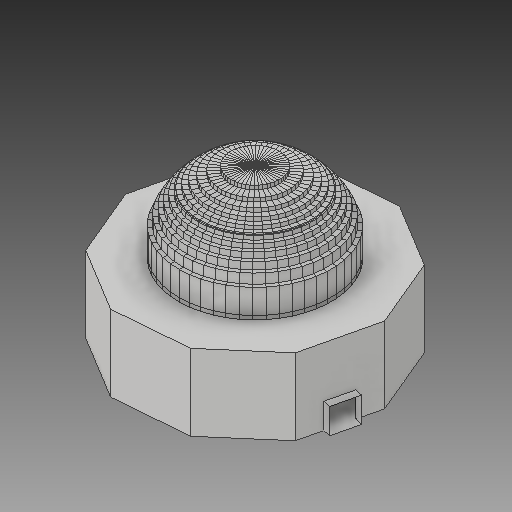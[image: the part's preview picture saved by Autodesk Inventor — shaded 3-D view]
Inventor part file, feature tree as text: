
AUTODESK INVENTOR PART (.ipt)
format: ipt  version: 2017 (Build 210142000, 142)  size: 2,418,176 bytes
history: native  units: in
note: dims shown in document units (in); Inventor stores cm internally (conversion verified against a paired STEP export)
features: extrude x8, sketch x7, other x3, plane x1, pattern_circular x1
ambient origin geometry x8: Origin, YZ Plane, XZ Plane, XY Plane, X Axis, Y Axis, Z Axis, Center Point
bodies: Solid1 (feature_tree)
feature tree (20):
  extrude  "bace"  Depth=1.0in TaperAngle=0.0deg
  extrude  "bace wall"  Depth=20.0in TaperAngle=0.0deg
  extrude  "bace ceiling"  Depth=1.0in
  other  "used to find the workplane for the dome"
  plane  "workplane for dome"
  extrude  "dome make"  Depth=1.0in TaperAngle=0.0deg
  sketch  "Sketch18"  dims[d190=45.0deg d192=1.0in d193=1.0in d194=1.0in d195=1.0in d196=1.0in d197=1.0in d198=1.0in d199=1.0in d200=0.0in d201=1.0in d202=0.0in d204=1.0in d205=19.685in d206=360.0deg d208=1.0in]
  extrude  "dome part cut 1"  Depth=2.5166in TaperAngle=90.0deg
  extrude  "dome part cut 2"  Depth=21.0in
  pattern_circular  "Circular Pattern6"  [2 undecoded]
  extrude  "door frame"  Depth=1.0in
  extrude  "corridor connection"  Depth=1.0in
  other  "Delete Faces of the room"
  other  "Delete Faces of dome"
  sketch  "Sketch1"  dims[d0=62.0in d1=1.0in d2=0.0in]
  sketch  "Sketch2"  dims[d4=1.0in d5=20.0in d6=0.0in]
  sketch  "Sketch3"  dims[d8=1.0in d9=0.0in d16=3.5in d17=6.6667in]
  sketch  "Sketch8"  dims[d18=1.0in d19=0.0in d107=1.0in d108=0.0in]
  sketch  "Sketch12"  dims[d109=40.0in d110=90.0deg d166=2.5166in]
  sketch  "Sketch17"  dims[d186=21.0in d187=0.0in d189=42.0in]
note: 2 required parameter values undecoded (feature->parameter linkage not recoverable at this tier; creation-order binding heuristic only, values carry confidence <= 0.55)
